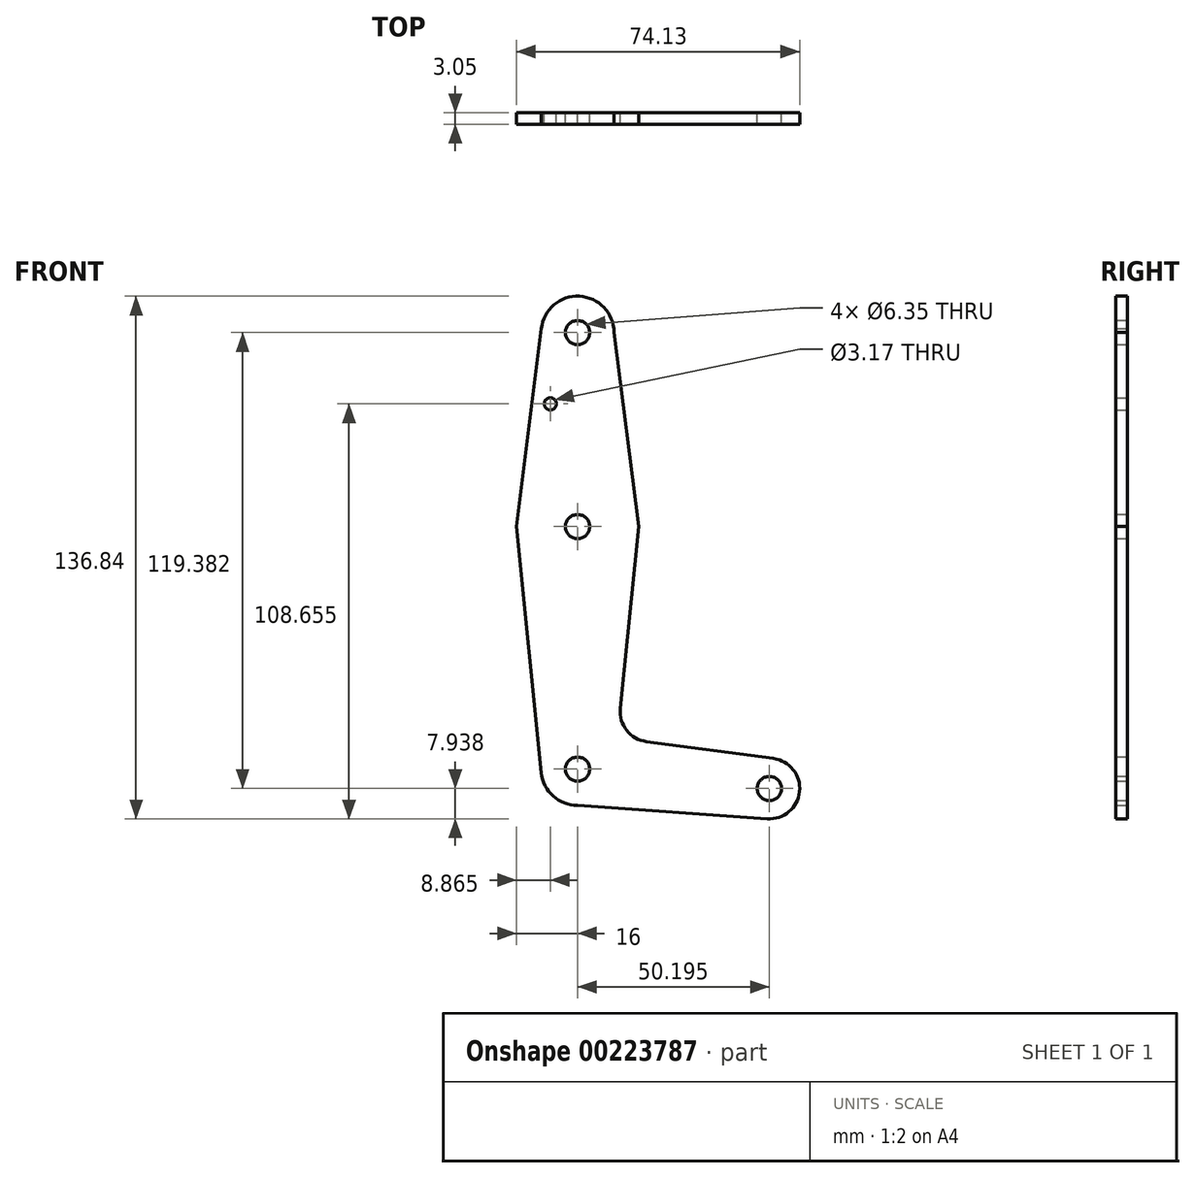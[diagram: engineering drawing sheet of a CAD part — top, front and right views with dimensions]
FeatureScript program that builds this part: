
annotation { "Feature Type Name" : "Feature", "Feature Type Description" : "" }
export const myFeature = defineFeature(function(context is Context, id is Id, definition is map)
    precondition{}
    {
        {
            var Q0;
            Q0=qCreatedBy(makeId("Front.planeOp"),FACE);
            var sketch = newSketch(context, id + "F0", { "sketchPlane" : qUnion([Q0])});
            skCircle(sketch, "E0", {"center": v(0, 50.8) * mm, "radius": 9.53 * mm});
            skCircle(sketch, "E1", {"center": v(0, 0) * mm, "radius": 15.88 * mm});
            skCircle(sketch, "E2", {"center": v(0, -63.5) * mm, "radius": 9.53 * mm});
            skCircle(sketch, "E3", {"center": v(50.2, -68.58) * mm, "radius": 7.94 * mm});
            skLineSegment(sketch, "E4", {"start": v(0, 50.8) * mm, "end": v(0, 0) * mm, "construction": true});
            skLineSegment(sketch, "E5", {"start": v(0, 0) * mm, "end": v(0, -63.5) * mm, "construction": true});
            skLineSegment(sketch, "E6", {"start": v(0, -63.5) * mm, "end": v(50.2, -68.58) * mm, "construction": true});
            skLineSegment(sketch, "E7", {"start": v(-9.43, 52.14) * mm, "end": v(-16, 0) * mm});
            skLineSegment(sketch, "E8", {"start": v(9.52, 50.88) * mm, "end": v(16, 0) * mm});
            skLineSegment(sketch, "E9", {"start": v(-16, 0) * mm, "end": v(-9.48, -64.46) * mm});
            skLineSegment(sketch, "E10", {"start": v(16, 0) * mm, "end": v(11.18, -47.61) * mm});
            skLineSegment(sketch, "E11", {"start": v(18.04, -56.3) * mm, "end": v(51.24, -60.71) * mm});
            skLineSegment(sketch, "E12", {"start": v(0, -73.03) * mm, "end": v(49.64, -76.5) * mm});
            skCircle(sketch, "E13", {"center": v(0, 50.8) * mm, "radius": 3.18 * mm});
            skCircle(sketch, "E14", {"center": v(0, 0) * mm, "radius": 3.18 * mm});
            skCircle(sketch, "E15", {"center": v(0, -63.5) * mm, "radius": 3.18 * mm});
            skCircle(sketch, "E16", {"center": v(50.2, -68.58) * mm, "radius": 3.18 * mm});
            skCircle(sketch, "E17", {"center": v(-7.13, 32.13) * mm, "radius": 1.59 * mm});
            skArc(sketch, "E18.filletArc", {"start": v(11.18, -47.61) * mm, "mid": v(12.85, -53.34) * mm, "end": v(18.04, -56.3) * mm});
            skSolve(sketch);
        }
        {
            var Q0;
            Q0 = qSketchRegion(id + "F0", true);
            extrude(context, id + "F1", {"entities" : qUnion([Q0]), "depth" : 3.05 * mm});
        }
    });
